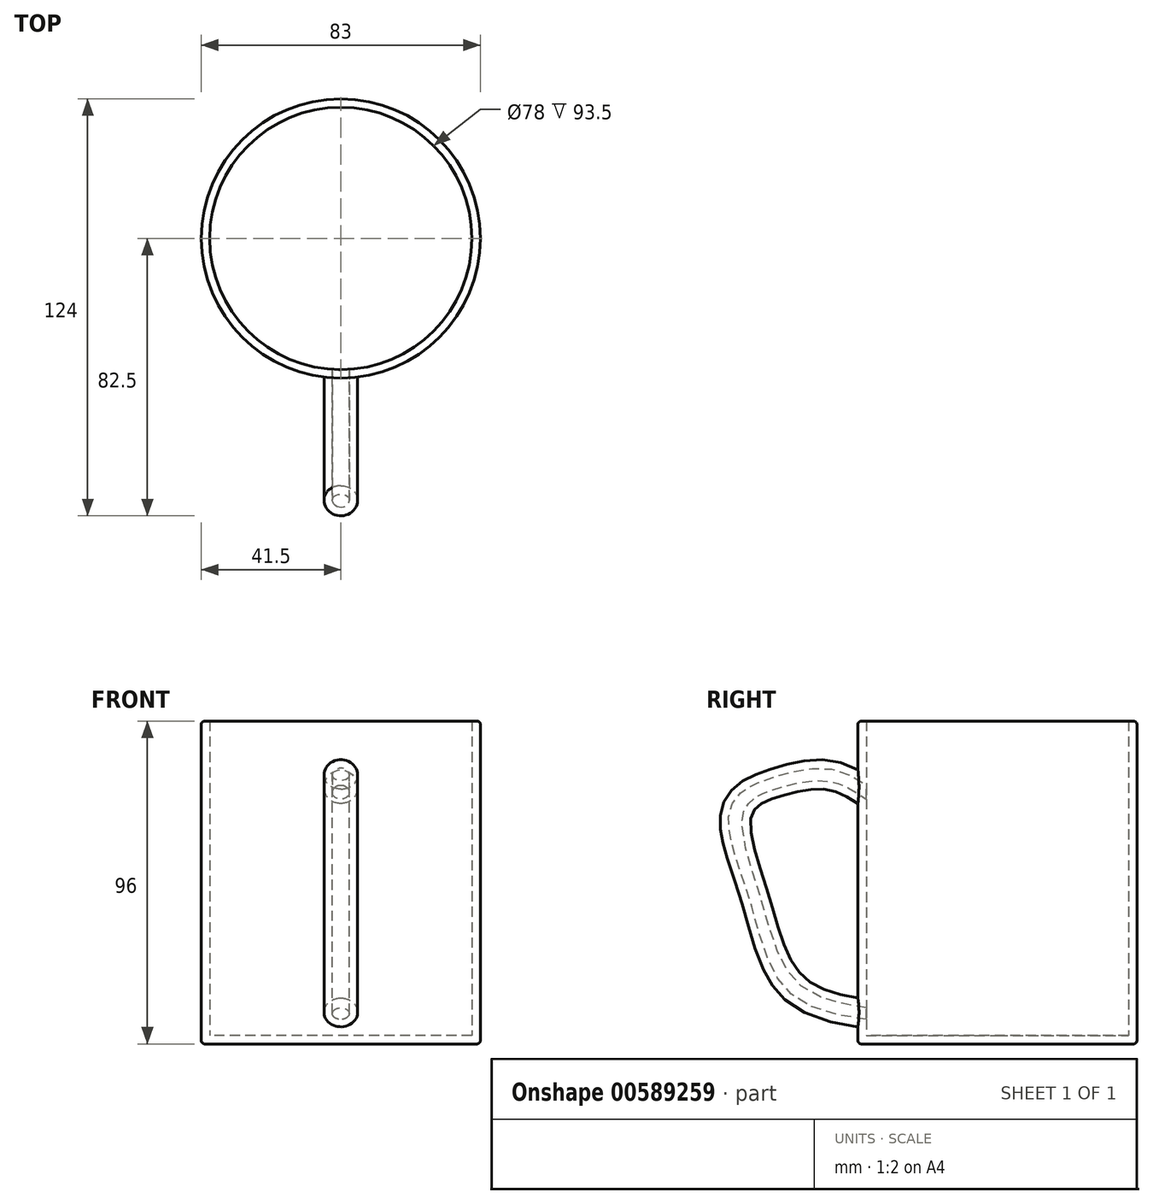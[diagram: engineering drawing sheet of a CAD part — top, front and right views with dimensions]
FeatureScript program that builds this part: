
annotation { "Feature Type Name" : "Feature", "Feature Type Description" : "" }
export const myFeature = defineFeature(function(context is Context, id is Id, definition is map)
    precondition{}
    {
        {
            var Q0;
            Q0=qCreatedBy(makeId("Top.planeOp"),FACE);
            var sketch = newSketch(context, id + "F0", { "sketchPlane" : qUnion([Q0])});
            skCircle(sketch, "E0", {"center": v(0, 0) * mm, "radius": 41.5 * mm});
            skSolve(sketch);
        }
        {
            var Q0;
            Q0 = qSketchRegion(id + "F0", true);
            extrude(context, id + "F1", {"entities" : qUnion([Q0]), "depth" : 96 * mm, "offsetDistance" : 25 * mm});
        }
        {
            var Q0;
            Q0=qCreatedBy(makeId("Right.planeOp"),FACE);
            var sketch = newSketch(context, id + "F2", { "sketchPlane" : qUnion([Q0])});
            skFitSpline(sketch, "E1", {"points": [v(-36.28, 69.4) * mm, v(-49.44, 76.82) * mm, v(-64.63, 75.13) * mm, v(-74.42, 68.72) * mm, v(-69.7, 44.76) * mm, v(-58.9, 19.1) * mm, v(-35.94, 11.34) * mm], "startDerivative": vector(-85.3, 65.24) * mm, "endDerivative": vector(140.84, -20.66) * mm});
            skSolve(sketch);
        }
        {
            var Q0;
            Q0=qCreatedBy(makeId("Front.planeOp"),FACE);
            cPlane(context, id + "F3", {"entities" : qUnion([Q0]), "cplaneType" : CPlaneType.OFFSET, "offset" : 41.5 * mm, "width" : 150 * mm, "height" : 150 * mm});
        }
        {
            var Q0;
            Q0=qCreatedBy(id+"F3.planeOp",FACE);
            var sketch = newSketch(context, id + "F4", { "sketchPlane" : qUnion([Q0])});
            skCircle(sketch, "E2", {"center": v(0, 76.48) * mm, "radius": 5 * mm});
            skSolve(sketch);
        }
        {
            var Q0;
            Q0=makeQuery(id+"F4.imprint","IMPRINT",FACE,{"disambiguationData":[TD([[makeQuery(id+"F4.imprint","IMPRINT",EDGE,{"derivedFrom":sQuery(id+"F4.wireOp",EDGE,"E2")}),1.0]])]});
            var Q1;
            Q1=sQuery(id+"F2.wireOp",EDGE,"E1");
            sweep(context, id + "F5", {"operationType" : NewBodyOperationType.ADD, "profiles" : qUnion([Q0]), "path" : qUnion([Q1])});
        }
        {
            var Q0;
            Q0=makeQuery(id+"F1.opExtrude","CAP_FACE",FACE,{"disambiguationData":[OSD([sQuery(id+"F0.wireOp",EDGE,"E0")])],"isStart":false});
            fillet(context, id + "F6", {"entities" : qUnion([Q0]), "radius" : 1 * mm, "tangentPropagation" : true, "allowEdgeOverflow" : false});
        }
        {
            var Q0;
            Q0=makeQuery(id+"F1.opExtrude","CAP_FACE",FACE,{"disambiguationData":[OSD([sQuery(id+"F0.wireOp",EDGE,"E0")])],"isStart":true});
            fillet(context, id + "F7", {"entities" : qUnion([Q0]), "radius" : 1 * mm, "tangentPropagation" : true, "allowEdgeOverflow" : false});
        }
        {
            var Q0;
            Q0=makeQuery(id+"F1.opExtrude","CAP_FACE",FACE,{"disambiguationData":[OSD([sQuery(id+"F0.wireOp",EDGE,"E0")])],"isStart":false});
            shell(context, id + "F8", {"entities" : qUnion([Q0]), "thickness" : 2.5 * mm});
        }
    });
